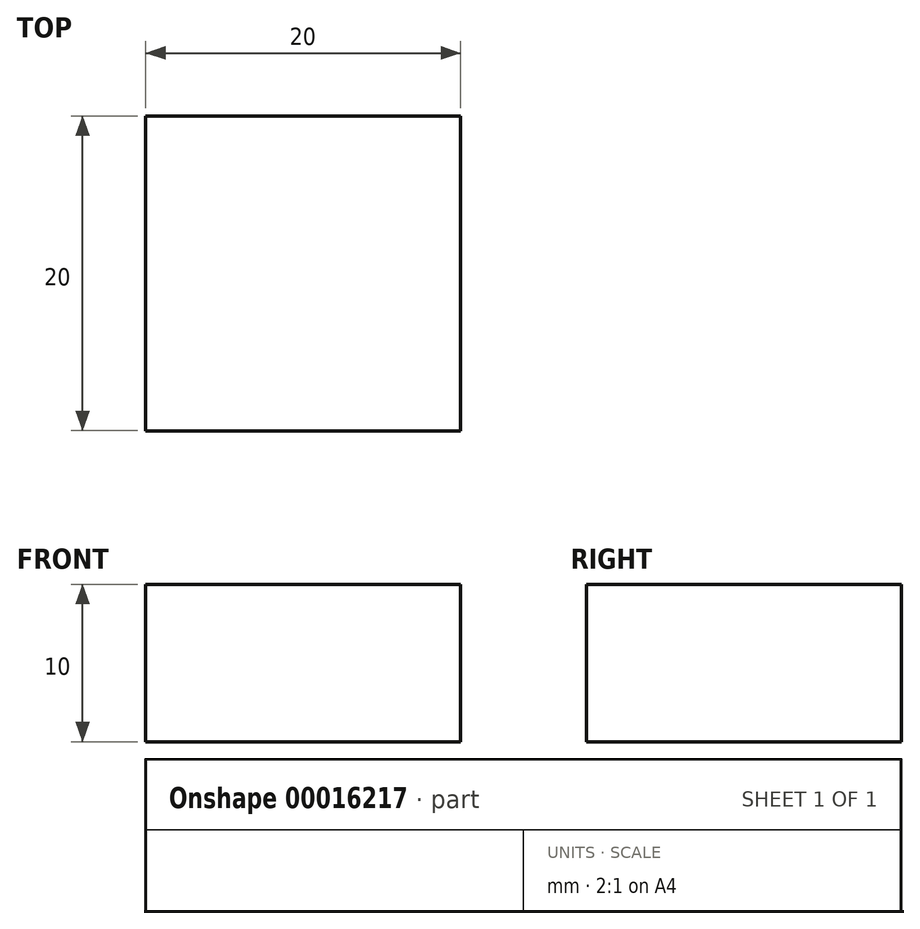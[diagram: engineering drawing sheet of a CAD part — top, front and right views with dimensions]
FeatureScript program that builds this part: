
annotation { "Feature Type Name" : "Feature", "Feature Type Description" : "" }
export const myFeature = defineFeature(function(context is Context, id is Id, definition is map)
    precondition{}
    {
        {
            var Q0;
            Q0=qCreatedBy(makeId("Top.planeOp"),FACE);
            var sketch = newSketch(context, id + "F0", { "sketchPlane" : qUnion([Q0])});
            skLineSegment(sketch, "E0.bottom", {"start": v(2.93, -17.9) * mm, "end": v(-17.07, -17.9) * mm});
            skLineSegment(sketch, "E0.top", {"start": v(2.93, 2.1) * mm, "end": v(-17.07, 2.1) * mm});
            skLineSegment(sketch, "E0.left", {"start": v(2.93, -17.9) * mm, "end": v(2.93, 2.1) * mm});
            skLineSegment(sketch, "E0.right", {"start": v(-17.07, -17.9) * mm, "end": v(-17.07, 2.1) * mm});
            skSolve(sketch);
        }
        {
            var Q0;
            Q0=makeQuery(id+"F0.imprint","IMPRINT",FACE,{"disambiguationData":[TD([[makeQuery(id+"F0.imprint","IMPRINT",EDGE,{"derivedFrom":sQuery(id+"F0.wireOp",EDGE,"E0.bottom")}),-1.0]])]});
            extrude(context, id + "F1", {"entities" : qUnion([Q0]), "depth" : 10 * mm});
        }
    });
